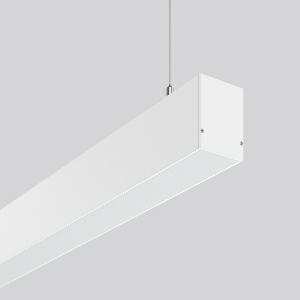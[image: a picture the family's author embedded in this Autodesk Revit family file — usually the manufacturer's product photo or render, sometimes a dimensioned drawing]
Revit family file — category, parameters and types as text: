
# Revit family: less_is_more_50_312311_002_76_395b
name_source: partatom
category: Lighting Fixtures
units: mm (PartAtom-declared; Revit-internal decimal feet)

## family parameters
Cut with Voids When Loaded = No
Host = Face
Light Source = No
Part Type = Normal
Room Calculation Point = No
Round Connector Dimension = Use Diameter
Shared = No

## types (1)
- LESS IS MORE 50 (1 x LED Modul 830, 2300 lm, 3000)
    Apparent Load = 22 VA
    CIE Flux Codes = 48 79 95 100 100
    Color Rendering = 80
    Color Temperature = 3000
    Default Elevation = 1800 mm
    Description = Series: LESS IS MORE 50
Linear pendant luminaire for aesthetically sophisticated lighting. Housing: extruded aluminium profile, powder-coated. End cap aluminium powder-coated. Canopy made of aluminium, powder-coated. Diffuser made of non-yellowing plastic (PMMA), opal. Direct light emission. Suitable for pendant. 2-point steel cable suspension freely positionable and infinitely height-adjustable. Special lengths available on request. LED unit with integrated converter interchangeable and removable. Suitable for through-wiring. With sensors or as a safety luminaire on request. 
Colour: traffic white, matt (RAL 9016)
Length: 847 mm
Width: 57 mm
Height: 75 mm
Suspension length: 2000 mm
Lamp: LED
Socket: without socket
Colour temperature: 3000K
Colour rendering index (CRI): 80
System power: 22 W
Rated luminous flux: 2300 lm
Luminous efficiency: 105 lm/W
Control gear: Converter, dimmable, DALI
Protection class: I
Type of protection: IP 20
    Height = 75 mm
    Lamp = 1 x LED Modul 830
    Lamp Light Flux = 2300 lm
    Lamp count = 1
    Length = 847 mm
    Lifetime = 50000 h
    Luminous efficacy = 105 lm/W
    Manufacturer = RZB
    ModVariant = No
    Model = 312311.002.76
    Mounting Place = Ceiling
    Mounting Type = Pendant
    Number of Poles = 1
    OnlyDefault = Yes
    Power Factor = 1
    Product Name = LESS IS MORE 50
    Product group = Pendant LED linear luminaires
    ProductGroupID = 907
    Protection Class = Protection class I
    Protection Degree = IP 20
    RLX_Detail_Level = 1
    RLX_Emergency_Light_Flux = 0 lm
    RLX_Emergency_Type = 0
    RLX_Emergency_Type_DB = No
    RlxData = <blob elided: 20633 chars, md5=d2405e53>
    Socket = socket
    Standby Power = 0 W
    System Light Flux = 2300 lm
    System Power = 22 W
    Type Comments = Product without accessories
    Type Image = 312318.002.jpg
    URL = http://relux.com
    VarID = ---
    Voltage = 230 V
    Voltage Range = 220-240 V
    Weight = 0.00 kg
    Width = 57 mm

## geometry (parser evidence)
native form markers: Blend x4, Sweep x11
no freeform markers — native parametric forms only
